# Revit family: Hager-Orion_Plus-IP65-D200-Cl.I-Steel_encl-630A-PT-pt
name_source: partatom
category: Equipement électrique
units: mm (PartAtom-declared; Revit-internal decimal feet)

## family parameters
Configuration du panneau = Deux colonnes, circuits au sein
Cote de connecteur circulaire = Utiliser le diamètre
Couper avec des vides une fois chargée = Non
Hôte = Face
Partagée = Non
Point de calcul de pièce = Non
Type d'élément = Tableau de raccordement

## types (2) — shared parameters
Commentaires du type = Orion Plus
EF000003 - Método de montagem = EV000384 - Montagem em superfície (gesso)
EF000007 - Cor = EV000270 - Cinzento
EF000008 - Largura = 500 mm  [stored 1.64042 ft]
EF000049 - Profundidade = 200 mm  [stored 0.656168 ft]
EF000116 - Número RAL = 7035
EF000118 - Com tampa de montagem = Non
EF000339 - Tipo de difusor = EV004216 - Porta
EF000437 - Número de entradas de condutores = 2
EF001088 - Extensão possível = Oui
EF001131 - Profundidade interior = 200 mm  [stored 0.656168 ft]
EF001596 - Material do corpo = EV000179 - Aço
EF001613 - Integridade do circuito = EV000494 - Nenhum
EF002950 - Largura em número de módulos = 22
EF003532 - Adequado para uso no exterior = Non
EF004293 - Força de impacto = EV008784 - IK10
EF004464 - Tipo de porta = EV002646 - Único
EF005474 - Grau de proteção (IP) = EV006421 - IP65
EF006244 - Tampa/porta transparente = Oui
EF006306 - Com fecho = Oui
EF007800 - Adequado para proteção contra raios = Non
EF008873 - Corrente nominal (In) = 630 A
EF009170 - Espessura do material do invólucro = 1 mm  [stored 0.00328084 ft]
EF009171 - Espessura do material da porta/tampa = 2 mm  [stored 0.00656168 ft]
EF009212 - Tipo de tampa = EV000116 - Fechado
EF009554 - Número de aberturas para placas de flange = 2
EF015940 - Tampa com libertação de sobrepressão = Non
Fabricant = Hager
HG000002 - Com porta ou tampa = Oui
HG000003 - Gama = Orion Plus
HG000006 - Encastrado = Non
HG000009 - Porta dupla = Non
HG000010 - Portas assimétricas = Non
HG000023 - Recinto de secção dupla = Non
HG000024 - Altura da secção inferior = 800 mm  [stored 2.62467 ft]
HG000026 - Instalação no chão = Non
zero-valued in all types: EF000218 - Profundidade incorporada, Elévation par défaut, HG000027 - Altura da Plinta

## per-type parameters (varying)
| type | EF000040 - Altura | EF000266 - Número de linhas | EF004427 - Número de módulos | HG000004 - Referência do Fabricante |
| Montagem em superfície (gesso) IP65 L500 A650 P200  - FL169A | 650 mm  [stored 2.13255 ft] | 4 | 96 | FL169A |
| Montagem em superfície (gesso) IP65 L500 A800 P200  - FL171A | 800 mm  [stored 2.62467 ft] | 5 | 110 | FL171A |

note: [stored X ft] marks values corroborated as IEEE doubles in the binary element streams (Revit-internal decimal feet)

## geometry (parser evidence)
native form markers: Sweep x6
no freeform markers — native parametric forms only
